AUTODESK INVENTOR PART (.ipt)
format: ipt  version: 2023.5 (Build 275446000, 446)  size: 105,472 bytes
history: native  units: in
note: dims shown in document units (in); Inventor stores cm internally (conversion verified against a paired STEP export)
features: sketch x2
ambient origin geometry x8: Origin, YZ Plane, XZ Plane, XY Plane, X Axis, Y Axis, Z Axis, Center Point
feature tree (2):
  sketch  "Sketch1"  dims[d0=2.0in]
  sketch  "Sketch2"  dims[d1=16.0in d2=0.75in d3=3.0in d4=5.0in d5=5.75in d6=2.0in d7=1.5in d8=8.0in d9=18.0in d10=11.75in d11=7.0in d12=6.5in d13=8.75in d14=8.75in d15=6.5in d16=5.0in d18=7.25in]
